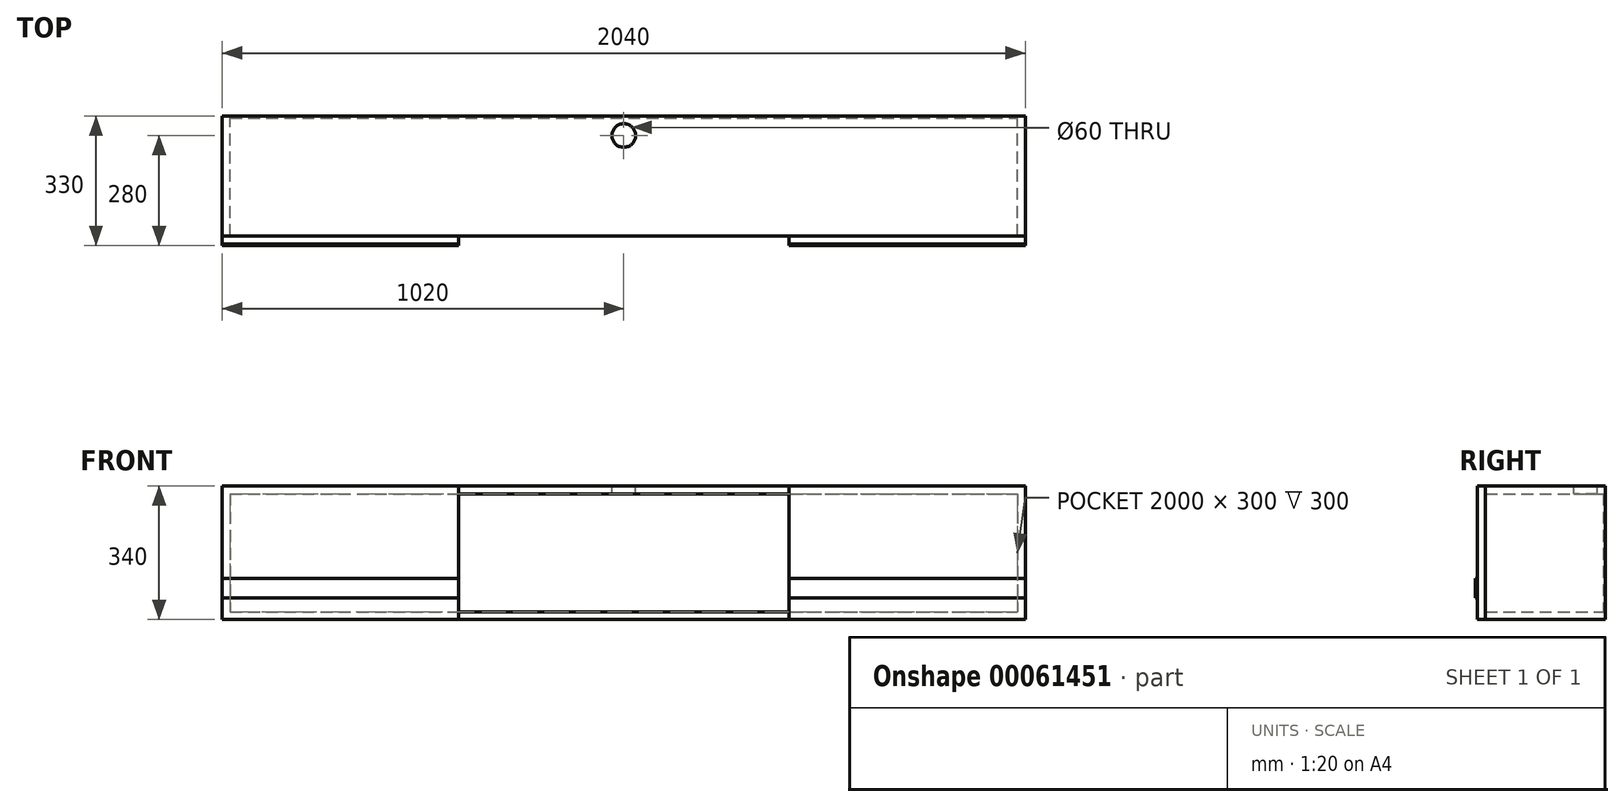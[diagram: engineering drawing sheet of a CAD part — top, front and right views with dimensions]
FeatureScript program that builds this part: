
annotation { "Feature Type Name" : "Feature", "Feature Type Description" : "" }
export const myFeature = defineFeature(function(context is Context, id is Id, definition is map)
    precondition{}
    {
        {
            var Q0;
            Q0=qCreatedBy(makeId("Front.planeOp"),FACE);
            var sketch = newSketch(context, id + "F0", { "sketchPlane" : qUnion([Q0])});
            skLineSegment(sketch, "E0.bottom", {"start": v(-1000, 300) * mm, "end": v(1000, 300) * mm});
            skLineSegment(sketch, "E0.top", {"start": v(-1000, 0) * mm, "end": v(1000, 0) * mm});
            skLineSegment(sketch, "E0.left", {"start": v(-1000, 300) * mm, "end": v(-1000, 0) * mm});
            skLineSegment(sketch, "E0.right", {"start": v(1000, 300) * mm, "end": v(1000, 0) * mm});
            skLineSegment(sketch, "E1.0", {"start": v(1020, 320) * mm, "end": v(1020, -20) * mm});
            skLineSegment(sketch, "E1.1", {"start": v(-1020, 320) * mm, "end": v(1020, 320) * mm});
            skLineSegment(sketch, "E1.2", {"start": v(-1020, 320) * mm, "end": v(-1020, -20) * mm});
            skLineSegment(sketch, "E1.3", {"start": v(-1020, -20) * mm, "end": v(1020, -20) * mm});
            skSolve(sketch);
        }
        {
            var Q0;
            Q0 = qSketchRegion(id + "F0", true);
            extrude(context, id + "F1", {"entities" : qUnion([Q0]), "depth" : 300 * mm});
        }
        {
            var Q0;
            Q0=makeQuery(id+"F1.opExtrude","CAP_FACE",FACE,{"disambiguationData":[OSD([sQuery(id+"F0.wireOp",EDGE,"E0.bottom"),sQuery(id+"F0.wireOp",EDGE,"E0.top"),sQuery(id+"F0.wireOp",EDGE,"E0.left"),sQuery(id+"F0.wireOp",EDGE,"E0.right"),sQuery(id+"F0.wireOp",EDGE,"E1.0"),sQuery(id+"F0.wireOp",EDGE,"E1.1"),sQuery(id+"F0.wireOp",EDGE,"E1.2"),sQuery(id+"F0.wireOp",EDGE,"E1.3")])],"isStart":true});
            var sketch = newSketch(context, id + "F2", { "sketchPlane" : qUnion([Q0])});
            skLineSegment(sketch, "E2.bottom", {"start": v(-1020, 320) * mm, "end": v(1020, 320) * mm});
            skLineSegment(sketch, "E2.top", {"start": v(-1020, -20) * mm, "end": v(1020, -20) * mm});
            skLineSegment(sketch, "E2.left", {"start": v(-1020, 320) * mm, "end": v(-1020, -20) * mm});
            skLineSegment(sketch, "E2.right", {"start": v(1020, 320) * mm, "end": v(1020, -20) * mm});
            skSolve(sketch);
        }
        {
            var Q0;
            Q0 = qSketchRegion(id + "F2", true);
            extrude(context, id + "F3", {"entities" : qUnion([Q0]), "operationType" : NewBodyOperationType.ADD, "depth" : 5 * mm});
        }
        {
            var Q0;
            Q0=makeQuery(id+"F1.opExtrude","CAP_FACE",FACE,{"disambiguationData":[OSD([sQuery(id+"F0.wireOp",EDGE,"E0.bottom"),sQuery(id+"F0.wireOp",EDGE,"E0.top"),sQuery(id+"F0.wireOp",EDGE,"E0.left"),sQuery(id+"F0.wireOp",EDGE,"E0.right"),sQuery(id+"F0.wireOp",EDGE,"E1.0"),sQuery(id+"F0.wireOp",EDGE,"E1.1"),sQuery(id+"F0.wireOp",EDGE,"E1.2"),sQuery(id+"F0.wireOp",EDGE,"E1.3")])],"isStart":false});
            var sketch = newSketch(context, id + "F4", { "sketchPlane" : qUnion([Q0])});
            skLineSegment(sketch, "E3.bottom", {"start": v(-1020, 320) * mm, "end": v(-420, 320) * mm});
            skLineSegment(sketch, "E3.top", {"start": v(-1020, -20) * mm, "end": v(-420, -20) * mm});
            skLineSegment(sketch, "E3.left", {"start": v(-1020, 320) * mm, "end": v(-1020, -20) * mm});
            skLineSegment(sketch, "E3.right", {"start": v(-420, 320) * mm, "end": v(-420, -20) * mm});
            skSolve(sketch);
        }
        {
            var Q0;
            Q0 = qSketchRegion(id + "F4", true);
            extrude(context, id + "F5", {"entities" : qUnion([Q0]), "depth" : 20 * mm});
        }
        {
            var Q0;
            Q0=makeQuery(id+"F5.opExtrude","SWEPT_BODY",BODY,{"disambiguationData":[OSD([sQuery(id+"F4.wireOp",EDGE,"E3.bottom"),sQuery(id+"F4.wireOp",EDGE,"E3.top"),sQuery(id+"F4.wireOp",EDGE,"E3.left"),sQuery(id+"F4.wireOp",EDGE,"E3.right")])]});
            var Q1;
            Q1=qCreatedBy(makeId("Right.planeOp"),FACE);
            mirror(context, id + "F6", {"entities" : qUnion([Q0]), "mirrorPlane" : qUnion([Q1])});
        }
        {
            var Q0;
            Q0=makeQuery(id+"F5.opExtrude","CAP_FACE",FACE,{"disambiguationData":[OSD([sQuery(id+"F4.wireOp",EDGE,"E3.bottom"),sQuery(id+"F4.wireOp",EDGE,"E3.top"),sQuery(id+"F4.wireOp",EDGE,"E3.left"),sQuery(id+"F4.wireOp",EDGE,"E3.right")])],"isStart":false});
            var sketch = newSketch(context, id + "F7", { "sketchPlane" : qUnion([Q0])});
            skLineSegment(sketch, "E4.bottom", {"start": v(-1020, 84.75) * mm, "end": v(-420, 84.75) * mm});
            skLineSegment(sketch, "E4.top", {"start": v(-1020, 34.75) * mm, "end": v(-420, 34.75) * mm});
            skLineSegment(sketch, "E4.left", {"start": v(-1020, 84.75) * mm, "end": v(-1020, 34.75) * mm});
            skLineSegment(sketch, "E4.right", {"start": v(-420, 84.75) * mm, "end": v(-420, 34.75) * mm});
            skSolve(sketch);
        }
        {
            var Q0;
            Q0 = qSketchRegion(id + "F7", true);
            extrude(context, id + "F8", {"entities" : qUnion([Q0]), "depth" : 5 * mm});
        }
        {
            var Q0;
            Q0=makeQuery(id+"F8.opExtrude","SWEPT_BODY",BODY,{"disambiguationData":[OSD([sQuery(id+"F7.wireOp",EDGE,"E4.bottom"),sQuery(id+"F7.wireOp",EDGE,"E4.top"),sQuery(id+"F7.wireOp",EDGE,"E4.left"),sQuery(id+"F7.wireOp",EDGE,"E4.right")])]});
            var Q1;
            Q1=qCreatedBy(makeId("Right.planeOp"),FACE);
            mirror(context, id + "F9", {"entities" : qUnion([Q0]), "mirrorPlane" : qUnion([Q1])});
        }
        {
            var Q0;
            Q0=makeQuery(id+"F3.boolean.opBoolean","MERGE",FACE,{"derivedFrom":[makeQuery(id+"F1.opExtrude","SWEPT_FACE",FACE,{"disambiguationData":[OSD([sQuery(id+"F0.wireOp",EDGE,"E1.1")])]}),makeQuery(id+"F3.opExtrude","SWEPT_FACE",FACE,{"disambiguationData":[OSD([sQuery(id+"F2.wireOp",EDGE,"E2.bottom")])]})]});
            var sketch = newSketch(context, id + "F10", { "sketchPlane" : qUnion([Q0])});
            skCircle(sketch, "E5", {"center": v(0, -45) * mm, "radius": 30 * mm});
            skLineSegment(sketch, "E6", {"start": v(-1020, -147.5) * mm, "end": v(1020, -147.5) * mm});
            skSolve(sketch);
        }
        {
            var Q0;
            Q0 = qSketchRegion(id + "F10", true);
            extrude(context, id + "F11", {"entities" : qUnion([Q0]), "operationType" : NewBodyOperationType.REMOVE, "oppositeDirection" : true, "depth" : 50 * mm});
        }
    });
